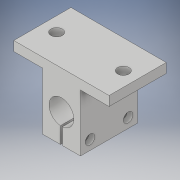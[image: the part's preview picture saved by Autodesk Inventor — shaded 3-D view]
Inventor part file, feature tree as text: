
AUTODESK INVENTOR PART (.ipt)
format: ipt  version: 2018 (Build 220112000, 112)  size: 154,624 bytes
history: native  units: mm
features: hole x4, sketch x3, extrude x2
ambient origin geometry x8: Origin, YZ Plane, XZ Plane, XY Plane, X Axis, Y Axis, Z Axis, Center Point
bodies: Solid1 (feature_tree)
feature tree (9):
  sketch  "3D Sketch1"
  extrude  "Extrusion1"  Depth=30.0mm TaperAngle=0.0deg
  hole  "Hole1"  [1 undecoded]
  hole  "Hole2"  [1 undecoded]
  extrude  "Extrusion2"  Depth=15.0mm
  hole  "Hole3"  [1 undecoded]
  hole  "Hole4"  [1 undecoded]
  sketch  "Sketch1"  dims[d2=13.0mm d4=30.0mm d5=0.0mm]
  sketch  "Sketch2"  dims[d6=5.0mm d7=5.0mm d8=3.0mm d9=6.0mm d10=5.0mm d11=3.0mm d12=90.0deg d13=8.0mm d14=20.594885mm d15=5.0mm d16=5.0mm d17=3.0mm d18=6.0mm d19=5.0mm d20=3.0mm d21=90.0deg d22=8.0mm d23=20.594885mm d24=3.0mm d25=0.0mm d26=15.0mm d28=15.0mm d29=15.0mm d30=7.5mm d31=6.0mm d32=6.0mm d33=4.0mm d34=2.0mm d35=90.0deg d36=8.0mm d37=20.594885mm d38=15.0mm d39=7.5mm d40=6.0mm d41=6.0mm d42=4.0mm d43=2.0mm d44=90.0deg d45=8.0mm d46=20.594885mm]
note: 4 required parameter values undecoded (feature->parameter linkage not recoverable at this tier; creation-order binding heuristic only, values carry confidence <= 0.55)
